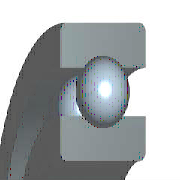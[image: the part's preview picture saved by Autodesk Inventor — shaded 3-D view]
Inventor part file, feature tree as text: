
AUTODESK INVENTOR PART (.ipt)
format: ipt  version: 2020 (Build 240168000, 168)  size: 358,912 bytes
history: native  units: mm (DEFAULTED — no unit token found)
features: sketch x1, other x1, pattern_circular x1
ambient origin geometry x8: Origin, YZ Plane, XZ Plane, XY Plane, X Axis, Y Axis, Z Axis, Center Point
bodies: Solid1 (feature_tree)
feature tree (3):
  sketch  "草图"  dims[d7=90.0deg d0=1.1mm d9=90.0deg d1=170.0mm d2=360.0deg d3=12.0mm d4=0.0mm d5=0.0mm d6=0.0mm d8=110.0mm d10=124.0mm d12=136.0mm d13=150.0mm d14=130.0mm d15=20.0mm d16=0.0mm d17=0.0mm]
  other  "轴承体"
  pattern_circular  "IDS_ARRAYBALL[SIMPL:T]"  [2 undecoded]
note: 2 required parameter values undecoded (feature->parameter linkage not recoverable at this tier; creation-order binding heuristic only, values carry confidence <= 0.55)
